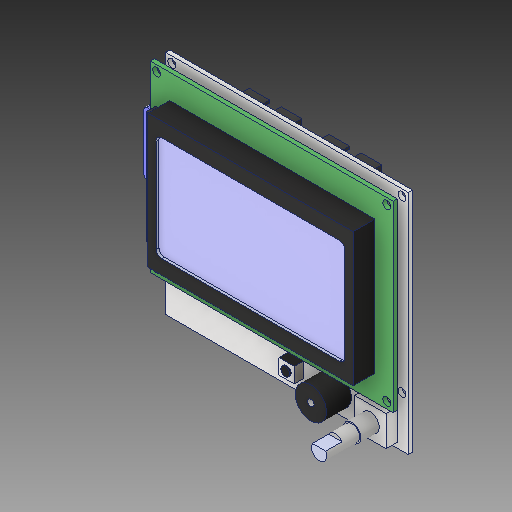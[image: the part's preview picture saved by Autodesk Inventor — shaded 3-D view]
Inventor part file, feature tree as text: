
AUTODESK INVENTOR PART (.ipt)
format: ipt  version: 2019 (Build 230136000, 136)  size: 206,336 bytes
history: native  units: mm
features: fillet x1
ambient origin geometry x8: Origin, YZ Plane, XZ Plane, XY Plane, X Axis, Y Axis, Z Axis, Center Point
bodies: Solid1 (feature_tree)
feature tree (1):
  fillet  "Fillet1 - SD Card"  [1 undecoded]
note: 1 required parameter value undecoded (feature->parameter linkage not recoverable at this tier; creation-order binding heuristic only, values carry confidence <= 0.55)
